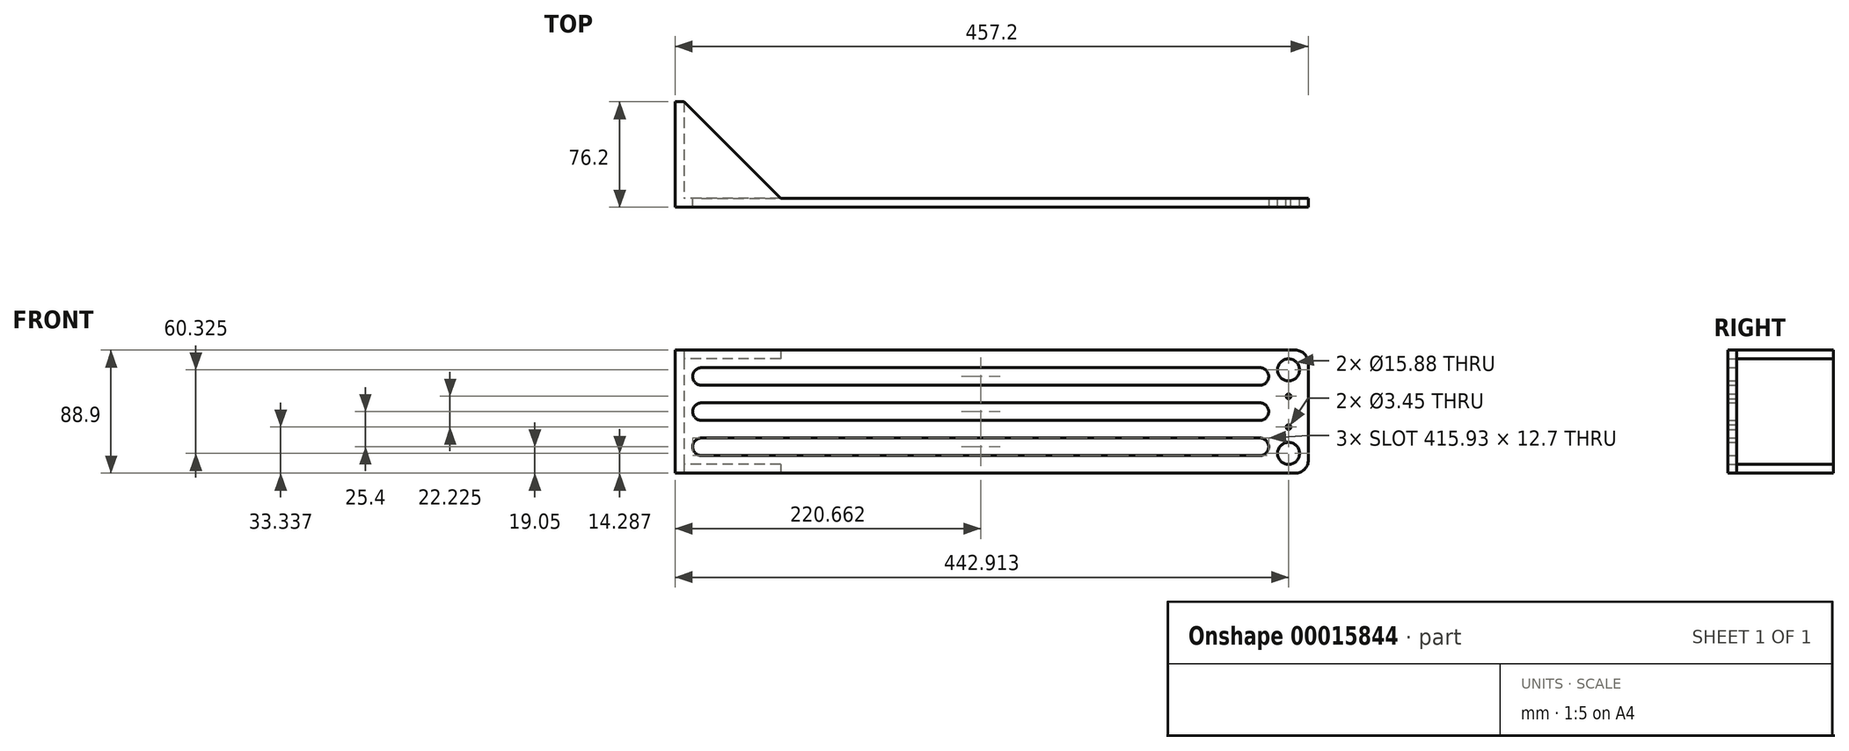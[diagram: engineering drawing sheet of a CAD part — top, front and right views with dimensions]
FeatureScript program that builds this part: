
annotation { "Feature Type Name" : "Feature", "Feature Type Description" : "" }
export const myFeature = defineFeature(function(context is Context, id is Id, definition is map)
    precondition{}
    {
        {
            var Q0;
            Q0=qCreatedBy(makeId("Top.planeOp"),FACE);
            var sketch = newSketch(context, id + "F0", { "sketchPlane" : qUnion([Q0])});
            skLineSegment(sketch, "E0.top", {"start": v(0, -76.2) * mm, "end": v(457.2, -76.2) * mm});
            skLineSegment(sketch, "E0.left", {"start": v(0, 0) * mm, "end": v(0, -76.2) * mm});
            skLineSegment(sketch, "E1.top", {"start": v(457.2, -69.85) * mm, "end": v(76.2, -69.85) * mm});
            skLineSegment(sketch, "E1.right", {"start": v(6.35, 0) * mm, "end": v(76.2, -69.85) * mm});
            skLineSegment(sketch, "E2", {"start": v(457.2, -76.2) * mm, "end": v(457.2, -69.85) * mm});
            skLineSegment(sketch, "E3", {"start": v(0, 0) * mm, "end": v(6.35, 0) * mm});
            skSolve(sketch);
        }
        {
            var Q0;
            Q0 = qSketchRegion(id + "F0", true);
            extrude(context, id + "F1", {"entities" : qUnion([Q0]), "depth" : 88.9 * mm});
        }
        {
            var Q0;
            Q0=makeQuery(id+"F1.opExtrude","SWEPT_FACE",FACE,{"disambiguationData":[OSD([sQuery(id+"F0.wireOp",EDGE,"E1.top")])]});
            var sketch = newSketch(context, id + "F2", { "sketchPlane" : qUnion([Q0])});
            skLineSegment(sketch, "E4.bottom", {"start": v(-76.2, 82.55) * mm, "end": v(-6.35, 82.55) * mm});
            skLineSegment(sketch, "E4.top", {"start": v(-76.2, 6.35) * mm, "end": v(-6.35, 6.35) * mm});
            skLineSegment(sketch, "E4.left", {"start": v(-76.2, 82.55) * mm, "end": v(-76.2, 6.35) * mm});
            skLineSegment(sketch, "E4.right", {"start": v(-6.35, 82.55) * mm, "end": v(-6.35, 6.35) * mm});
            skPoint(sketch, "E5", {"position": v(-76.2, 44.45) * mm});
            skSolve(sketch);
        }
        {
            var Q0;
            Q0 = qSketchRegion(id + "F2", true);
            var Q1;
            Q1=makeQuery(id+"F1.opExtrude","SWEPT_FACE",FACE,{"disambiguationData":[OSD([sQuery(id+"F0.wireOp",EDGE,"E1.right")])]});
            extrude(context, id + "F3", {"entities" : qUnion([Q0]), "operationType" : NewBodyOperationType.REMOVE, "endBound" : BoundingType.UP_TO_SURFACE, "endBoundEntityFace" : qUnion([Q1]), "depth" : 25.4 * mm});
        }
        {
            var Q0;
            Q0=makeQuery(id+"F3.boolean.opBoolean","MERGE",FACE,{"derivedFrom":[makeQuery(id+"F1.opExtrude","SWEPT_FACE",FACE,{"disambiguationData":[OSD([sQuery(id+"F0.wireOp",EDGE,"E1.top")])]}),makeQuery(id+"F3.opExtrude","CAP_FACE",FACE,{"disambiguationData":[OSD([sQuery(id+"F2.wireOp",EDGE,"E4.bottom"),sQuery(id+"F2.wireOp",EDGE,"E4.top"),sQuery(id+"F2.wireOp",EDGE,"E4.left"),sQuery(id+"F2.wireOp",EDGE,"E4.right")])],"isStart":true})]});
            var sketch = newSketch(context, id + "F4", { "sketchPlane" : qUnion([Q0])});
            skLineSegment(sketch, "E6.top", {"start": v(-457.2, 74.61) * mm, "end": v(-442.91, 74.61) * mm, "construction": true});
            skLineSegment(sketch, "E6.right", {"start": v(-442.91, 88.9) * mm, "end": v(-442.91, 74.61) * mm, "construction": true});
            skLineSegment(sketch, "E7.right", {"start": v(-442.91, 0) * mm, "end": v(-442.91, 14.29) * mm, "construction": true});
            skCircle(sketch, "E8", {"center": v(-442.91, 74.61) * mm, "radius": 7.94 * mm});
            skCircle(sketch, "E9", {"center": v(-442.91, 14.29) * mm, "radius": 7.94 * mm});
            skLineSegment(sketch, "E10", {"start": v(-442.91, 14.29) * mm, "end": v(-442.91, 33.34) * mm, "construction": true});
            skLineSegment(sketch, "E11", {"start": v(-442.91, 33.34) * mm, "end": v(-442.91, 55.56) * mm, "construction": true});
            skLineSegment(sketch, "E12", {"start": v(-442.91, 55.56) * mm, "end": v(-442.91, 74.61) * mm, "construction": true});
            skCircle(sketch, "E13", {"center": v(-442.91, 55.56) * mm, "radius": 1.73 * mm});
            skCircle(sketch, "E14", {"center": v(-442.91, 33.34) * mm, "radius": 1.73 * mm});
            skLineSegment(sketch, "E15", {"start": v(-76.2, 82.55) * mm, "end": v(-76.2, 76.2) * mm, "construction": true});
            skLineSegment(sketch, "E16.bottom", {"start": v(-12.7, 76.2) * mm, "end": v(-428.63, 76.2) * mm});
            skLineSegment(sketch, "E16.top", {"start": v(-12.7, 63.5) * mm, "end": v(-428.63, 63.5) * mm});
            skLineSegment(sketch, "E16.left", {"start": v(-12.7, 76.2) * mm, "end": v(-12.7, 63.5) * mm});
            skLineSegment(sketch, "E16.right", {"start": v(-428.63, 76.2) * mm, "end": v(-428.63, 63.5) * mm});
            skLineSegment(sketch, "E17", {"start": v(-12.7, 69.85) * mm, "end": v(-6.35, 69.85) * mm, "construction": true});
            skLineSegment(sketch, "E18", {"start": v(-442.91, 74.61) * mm, "end": v(-428.63, 74.61) * mm, "construction": true});
            skLineSegment(sketch, "E19", {"start": v(-220.66, 63.5) * mm, "end": v(-220.66, 50.8) * mm, "construction": true});
            skLineSegment(sketch, "E20.bottom", {"start": v(-12.7, 50.8) * mm, "end": v(-428.63, 50.8) * mm});
            skLineSegment(sketch, "E20.top", {"start": v(-12.7, 38.1) * mm, "end": v(-428.63, 38.1) * mm});
            skLineSegment(sketch, "E20.left", {"start": v(-12.7, 50.8) * mm, "end": v(-12.7, 38.1) * mm});
            skLineSegment(sketch, "E20.right", {"start": v(-428.63, 50.8) * mm, "end": v(-428.63, 38.1) * mm});
            skLineSegment(sketch, "E21", {"start": v(-220.66, 38.1) * mm, "end": v(-220.66, 25.4) * mm, "construction": true});
            skLineSegment(sketch, "E22.bottom", {"start": v(-428.63, 25.4) * mm, "end": v(-12.7, 25.4) * mm});
            skLineSegment(sketch, "E22.top", {"start": v(-428.63, 12.7) * mm, "end": v(-12.7, 12.7) * mm});
            skLineSegment(sketch, "E22.left", {"start": v(-428.63, 25.4) * mm, "end": v(-428.63, 12.7) * mm});
            skLineSegment(sketch, "E22.right", {"start": v(-12.7, 25.4) * mm, "end": v(-12.7, 12.7) * mm});
            skSolve(sketch);
        }
        {
            var Q0;
            Q0 = qSketchRegion(id + "F4", true);
            var Q1;
            Q1=makeQuery(id+"F1.opExtrude","SWEPT_FACE",FACE,{"disambiguationData":[OSD([sQuery(id+"F0.wireOp",EDGE,"E0.top")])]});
            extrude(context, id + "F5", {"entities" : qUnion([Q0]), "operationType" : NewBodyOperationType.REMOVE, "endBound" : BoundingType.UP_TO_SURFACE, "oppositeDirection" : true, "endBoundEntityFace" : qUnion([Q1]), "depth" : 25.4 * mm});
        }
        {
            var Q0;
            Q0=makeQuery(id+"F5.boolean.opBoolean","COPY",EDGE,{"derivedFrom":makeQuery(id+"F5.opExtrude","SWEPT_EDGE",EDGE,{"disambiguationData":[OSD([sQuery(id+"F4.wireOp",EDGE,"E16.bottom"),sQuery(id+"F4.wireOp",EDGE,"E16.left")])]})});
            var Q1;
            Q1=makeQuery(id+"F5.boolean.opBoolean","COPY",EDGE,{"derivedFrom":makeQuery(id+"F5.opExtrude","SWEPT_EDGE",EDGE,{"disambiguationData":[OSD([sQuery(id+"F4.wireOp",EDGE,"E16.top"),sQuery(id+"F4.wireOp",EDGE,"E16.left")])]})});
            var Q2;
            Q2=makeQuery(id+"F5.boolean.opBoolean","COPY",EDGE,{"derivedFrom":makeQuery(id+"F5.opExtrude","SWEPT_EDGE",EDGE,{"disambiguationData":[OSD([sQuery(id+"F4.wireOp",EDGE,"E20.bottom"),sQuery(id+"F4.wireOp",EDGE,"E20.left")])]})});
            var Q3;
            Q3=makeQuery(id+"F5.boolean.opBoolean","COPY",EDGE,{"derivedFrom":makeQuery(id+"F5.opExtrude","SWEPT_EDGE",EDGE,{"disambiguationData":[OSD([sQuery(id+"F4.wireOp",EDGE,"E20.top"),sQuery(id+"F4.wireOp",EDGE,"E20.left")])]})});
            var Q4;
            Q4=makeQuery(id+"F5.boolean.opBoolean","COPY",EDGE,{"derivedFrom":makeQuery(id+"F5.opExtrude","SWEPT_EDGE",EDGE,{"disambiguationData":[OSD([sQuery(id+"F4.wireOp",EDGE,"E22.top"),sQuery(id+"F4.wireOp",EDGE,"E22.right")])]})});
            var Q5;
            Q5=makeQuery(id+"F5.boolean.opBoolean","COPY",EDGE,{"derivedFrom":makeQuery(id+"F5.opExtrude","SWEPT_EDGE",EDGE,{"disambiguationData":[OSD([sQuery(id+"F4.wireOp",EDGE,"E22.bottom"),sQuery(id+"F4.wireOp",EDGE,"E22.right")])]})});
            var Q6;
            Q6=makeQuery(id+"F5.boolean.opBoolean","COPY",EDGE,{"derivedFrom":makeQuery(id+"F5.opExtrude","SWEPT_EDGE",EDGE,{"disambiguationData":[OSD([sQuery(id+"F4.wireOp",EDGE,"E22.top"),sQuery(id+"F4.wireOp",EDGE,"E22.left")])]})});
            var Q7;
            Q7=makeQuery(id+"F5.boolean.opBoolean","COPY",EDGE,{"derivedFrom":makeQuery(id+"F5.opExtrude","SWEPT_EDGE",EDGE,{"disambiguationData":[OSD([sQuery(id+"F4.wireOp",EDGE,"E20.top"),sQuery(id+"F4.wireOp",EDGE,"E20.right")])]})});
            var Q8;
            Q8=makeQuery(id+"F5.boolean.opBoolean","COPY",EDGE,{"derivedFrom":makeQuery(id+"F5.opExtrude","SWEPT_EDGE",EDGE,{"disambiguationData":[OSD([sQuery(id+"F4.wireOp",EDGE,"E16.top"),sQuery(id+"F4.wireOp",EDGE,"E16.right")])]})});
            var Q9;
            Q9=makeQuery(id+"F5.boolean.opBoolean","COPY",EDGE,{"derivedFrom":makeQuery(id+"F5.opExtrude","SWEPT_EDGE",EDGE,{"disambiguationData":[OSD([sQuery(id+"F4.wireOp",EDGE,"E16.bottom"),sQuery(id+"F4.wireOp",EDGE,"E16.right")])]})});
            var Q10;
            Q10=makeQuery(id+"F5.boolean.opBoolean","COPY",EDGE,{"derivedFrom":makeQuery(id+"F5.opExtrude","SWEPT_EDGE",EDGE,{"disambiguationData":[OSD([sQuery(id+"F4.wireOp",EDGE,"E20.bottom"),sQuery(id+"F4.wireOp",EDGE,"E20.right")])]})});
            var Q11;
            Q11=makeQuery(id+"F5.boolean.opBoolean","COPY",EDGE,{"derivedFrom":makeQuery(id+"F5.opExtrude","SWEPT_EDGE",EDGE,{"disambiguationData":[OSD([sQuery(id+"F4.wireOp",EDGE,"E22.bottom"),sQuery(id+"F4.wireOp",EDGE,"E22.left")])]})});
            fillet(context, id + "F6", {"entities" : qUnion([Q0, Q1, Q2, Q3, Q4, Q5, Q6, Q7, Q8, Q9, Q10, Q11]), "radius" : 6.35 * mm, "tangentPropagation" : true, "allowEdgeOverflow" : false});
        }
        {
            var Q0;
            Q0=makeQuery(id+"F1.opExtrude","CAP_EDGE",EDGE,{"disambiguationData":[OSD([sQuery(id+"F0.wireOp",EDGE,"E2")])],"isStart":false});
            var Q1;
            Q1=makeQuery(id+"F1.opExtrude","CAP_EDGE",EDGE,{"disambiguationData":[OSD([sQuery(id+"F0.wireOp",EDGE,"E2")])],"isStart":true});
            fillet(context, id + "F7", {"entities" : qUnion([Q0, Q1]), "radius" : 9.52 * mm, "tangentPropagation" : true, "allowEdgeOverflow" : false});
        }
    });
